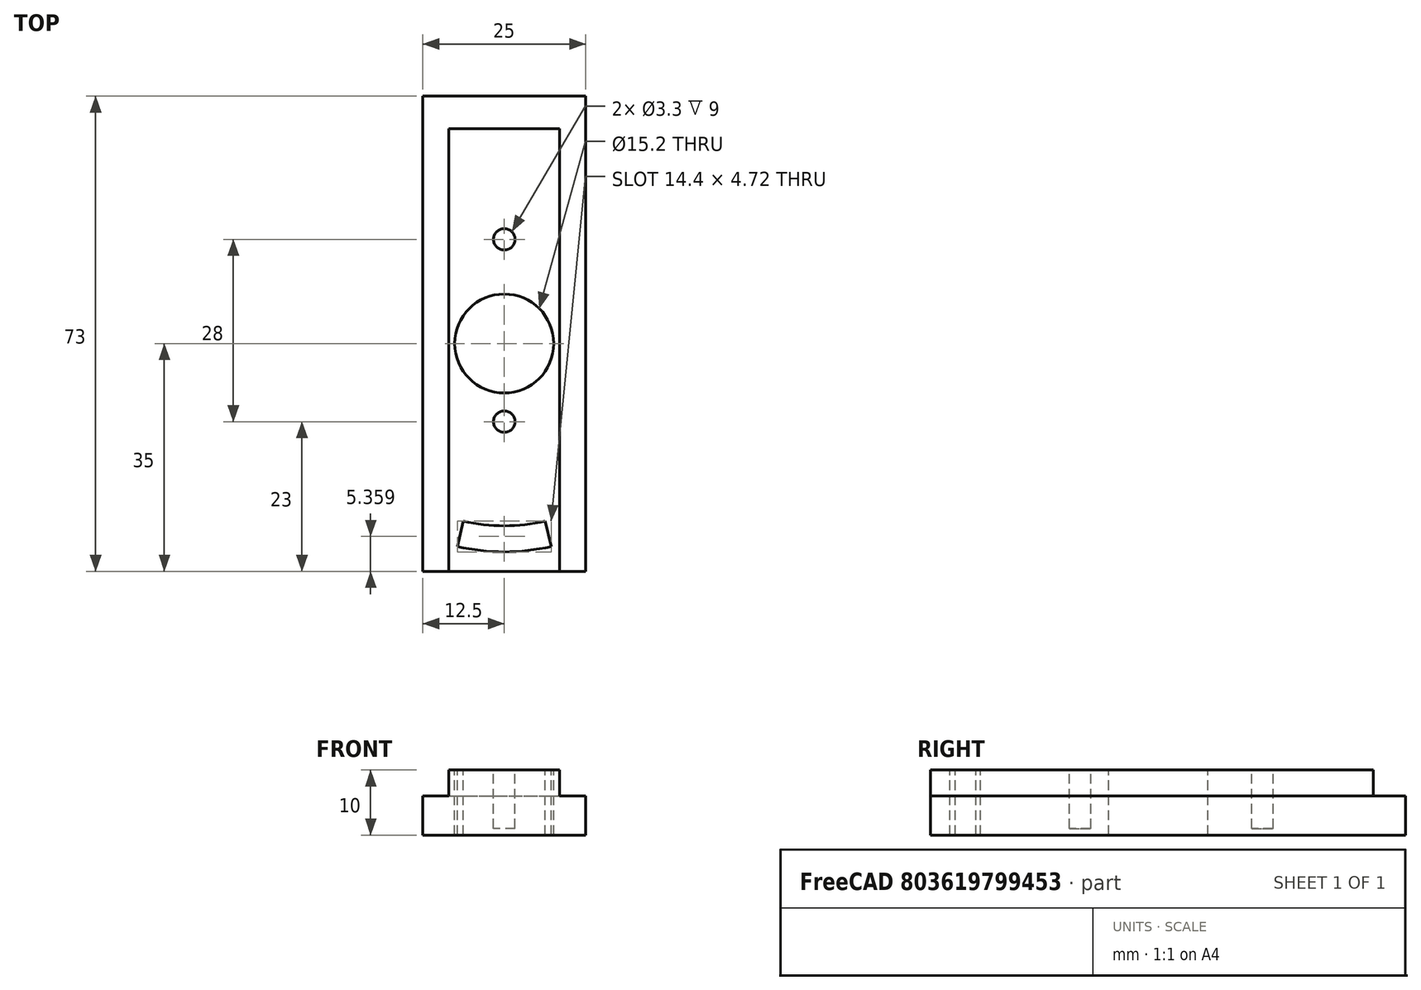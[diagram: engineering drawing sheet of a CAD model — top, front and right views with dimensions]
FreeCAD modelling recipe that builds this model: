
FCSTD DOCUMENT  (FreeCAD 0.18R4 (GitTag))
Label: Kamerhalter_Teil_3
License: All rights reserved
LicenseURL: http://en.wikipedia.org/wiki/All_rights_reserved
objects: Part::Cylinder×5, Part::Box×4, Part::Cut×2, Part::MultiFuse×2
note: 13 computed .brp shape members not serialized (recipe doc carries the construction recipe); baked Part::Feature solids carry a one-line shape summary decoded from their .brp

FEATURE [Part::Cylinder] Cylinder002  label="Zylinder001"
  Angle = 26
  AttacherType = Attacher::AttachEngine3D
  Height = 10
  Placement = pos=(0,0,0) rot=(0,0,-1;1.79769rad)
  Radius = 32
FEATURE [Part::Cylinder] Cylinder003  label="Zylinder002"
  Angle = 26
  AttacherType = Attacher::AttachEngine3D
  Height = 10
  Placement = pos=(0,0,0) rot=(0,0,-1;1.79769rad)
  Radius = 28
FEATURE [Part::Box] Box001  label="Würfel001"
  AttacherType = Attacher::AttachEngine3D
  Height = 10
  Length = 25
  Placement = pos=(-12.5,-35,0) rot=(0,0,1;0rad)
  Width = 68
FEATURE [Part::Cut] Cut001
  Base = -> Cylinder002
  Tool = -> Cylinder003
FEATURE [Part::Cylinder] Cylinder  label="Zylinder"
  Angle = 360
  AttacherType = Attacher::AttachEngine3D
  Height = 10
  Radius = 7.6
FEATURE [Part::Cylinder] Cylinder004  label="Zylinder003"
  Angle = 360
  AttacherType = Attacher::AttachEngine3D
  Height = 9
  Placement = pos=(0,-12,1) rot=(0,0,1;0rad)
  Radius = 1.65
FEATURE [Part::Cylinder] Cylinder005  label="Zylinder004"
  Angle = 360
  AttacherType = Attacher::AttachEngine3D
  Height = 9
  Placement = pos=(0,16,1) rot=(0,0,1;0rad)
  Radius = 1.65
FEATURE [Part::Box] Box  label="Würfel002"
  AttacherType = Attacher::AttachEngine3D
  Height = 4
  Length = 4
  Placement = pos=(8.5,-35,6) rot=(0,0,1;0rad)
  Width = 68
FEATURE [Part::Box] Box002  label="Würfel003"
  AttacherType = Attacher::AttachEngine3D
  Height = 4
  Length = 4
  Placement = pos=(-12.5,-35,6) rot=(0,0,1;0rad)
  Width = 68
FEATURE [Part::MultiFuse] Fusion
  Shapes = -> [Cut001,Cylinder,Cylinder004,Cylinder005,Box,Box002]
FEATURE [Part::Cut] Cut
  Base = -> Box001
  Tool = -> Fusion
FEATURE [Part::Box] Box003  label="Würfel"
  AttacherType = Attacher::AttachEngine3D
  Height = 6
  Length = 25
  Placement = pos=(-12.5,33,0) rot=(0,0,1;0rad)
  Width = 5
FEATURE [Part::MultiFuse] Fusion001
  Shapes = -> [Cut,Box003]
